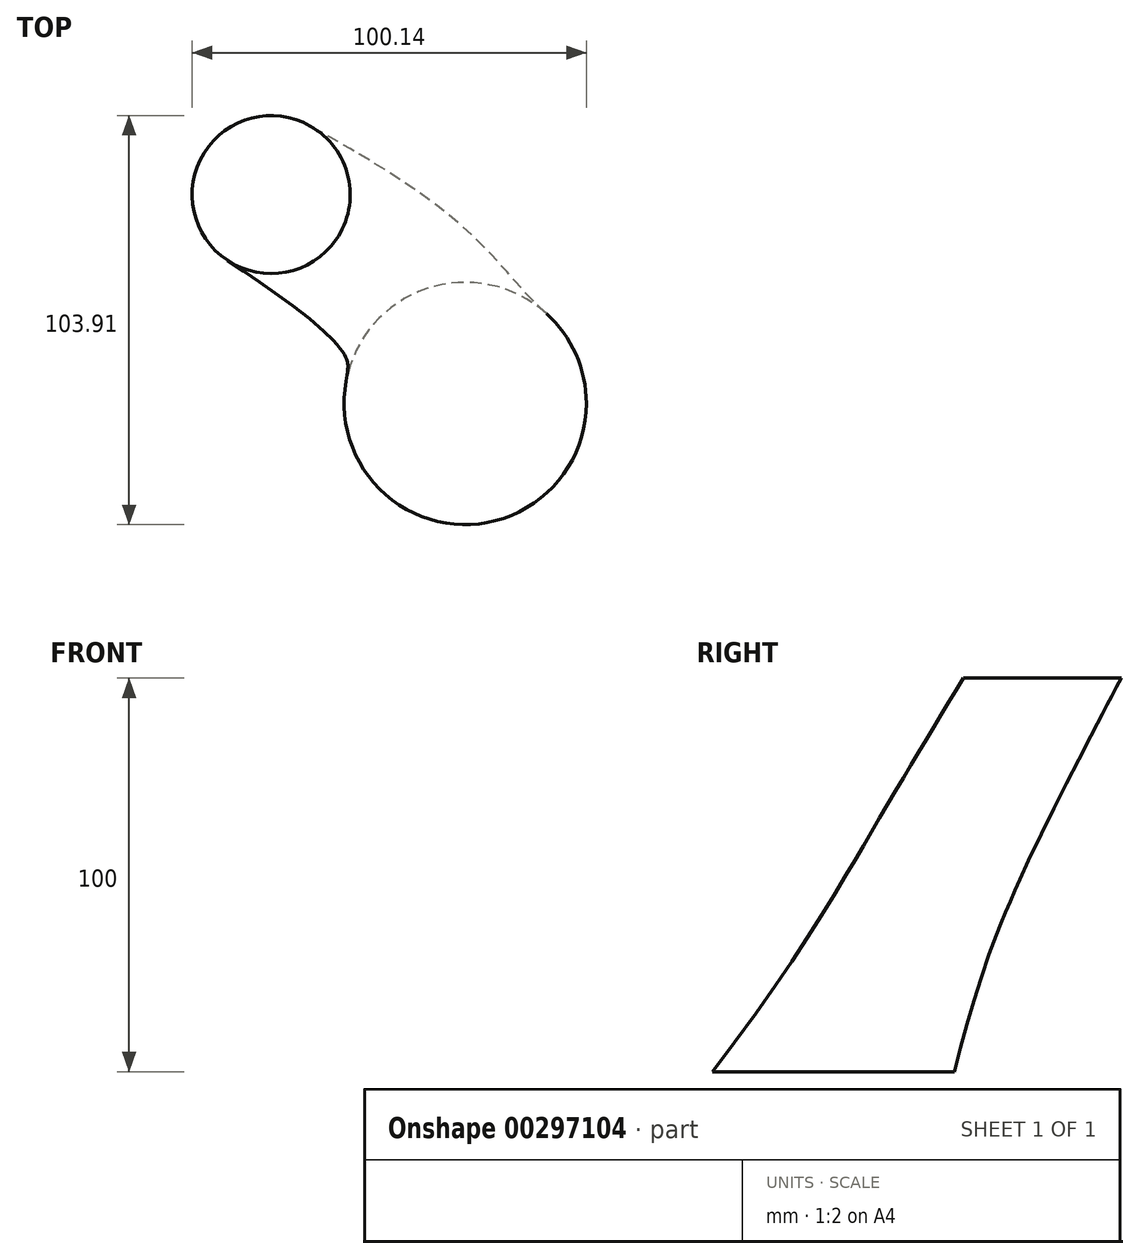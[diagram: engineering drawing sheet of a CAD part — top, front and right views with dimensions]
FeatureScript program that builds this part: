
annotation { "Feature Type Name" : "Feature", "Feature Type Description" : "" }
export const myFeature = defineFeature(function(context is Context, id is Id, definition is map)
    precondition{}
    {
        {
            var Q0;
            Q0=qCreatedBy(makeId("Top.planeOp"),FACE);
            var sketch = newSketch(context, id + "F0", { "sketchPlane" : qUnion([Q0])});
            skCircle(sketch, "E0", {"center": v(0, 0) * mm, "radius": 30.77 * mm});
            skSolve(sketch);
        }
        {
            var Q0;
            Q0=qCreatedBy(makeId("Top.planeOp"),FACE);
            cPlane(context, id + "F1", {"entities" : qUnion([Q0]), "cplaneType" : CPlaneType.OFFSET, "offset" : 50 * mm, "width" : 150 * mm, "height" : 150 * mm});
        }
        {
            var Q0;
            Q0=qCreatedBy(id+"F1.planeOp",FACE);
            var sketch = newSketch(context, id + "F2", { "sketchPlane" : qUnion([Q0])});
            skCircle(sketch, "E1", {"center": v(-12.61, 25.58) * mm, "radius": 22.32 * mm});
            skSolve(sketch);
        }
        {
            var Q0;
            Q0=qCreatedBy(id+"F1.planeOp",FACE);
            cPlane(context, id + "F3", {"entities" : qUnion([Q0]), "cplaneType" : CPlaneType.OFFSET, "offset" : 50 * mm, "width" : 150 * mm, "height" : 150 * mm});
        }
        {
            var Q0;
            Q0=qCreatedBy(id+"F3.planeOp",FACE);
            var sketch = newSketch(context, id + "F4", { "sketchPlane" : qUnion([Q0])});
            skCircle(sketch, "E2", {"center": v(-49.3, 53.07) * mm, "radius": 20.07 * mm});
            skSolve(sketch);
        }
        {
            var Q0;
            Q0=makeQuery(id+"F0.imprint","IMPRINT",FACE,{"disambiguationData":[TD([[makeQuery(id+"F0.imprint","IMPRINT",EDGE,{"derivedFrom":sQuery(id+"F0.wireOp",EDGE,"E0")}),1.0]])]});
            var Q1;
            Q1=makeQuery(id+"F2.imprint","IMPRINT",FACE,{"disambiguationData":[TD([[makeQuery(id+"F2.imprint","IMPRINT",EDGE,{"derivedFrom":sQuery(id+"F2.wireOp",EDGE,"E1")}),1.0]])]});
            var Q2;
            Q2=makeQuery(id+"F4.imprint","IMPRINT",FACE,{"disambiguationData":[TD([[makeQuery(id+"F4.imprint","IMPRINT",EDGE,{"derivedFrom":sQuery(id+"F4.wireOp",EDGE,"E2")}),1.0]])]});
            loft(context, id + "F5", {"sheetProfilesArray" : [{ "sheetProfileEntities" : qUnion([Q0]) }, { "sheetProfileEntities" : qUnion([Q1]) }, { "sheetProfileEntities" : qUnion([Q2]) }]});
        }
    });
